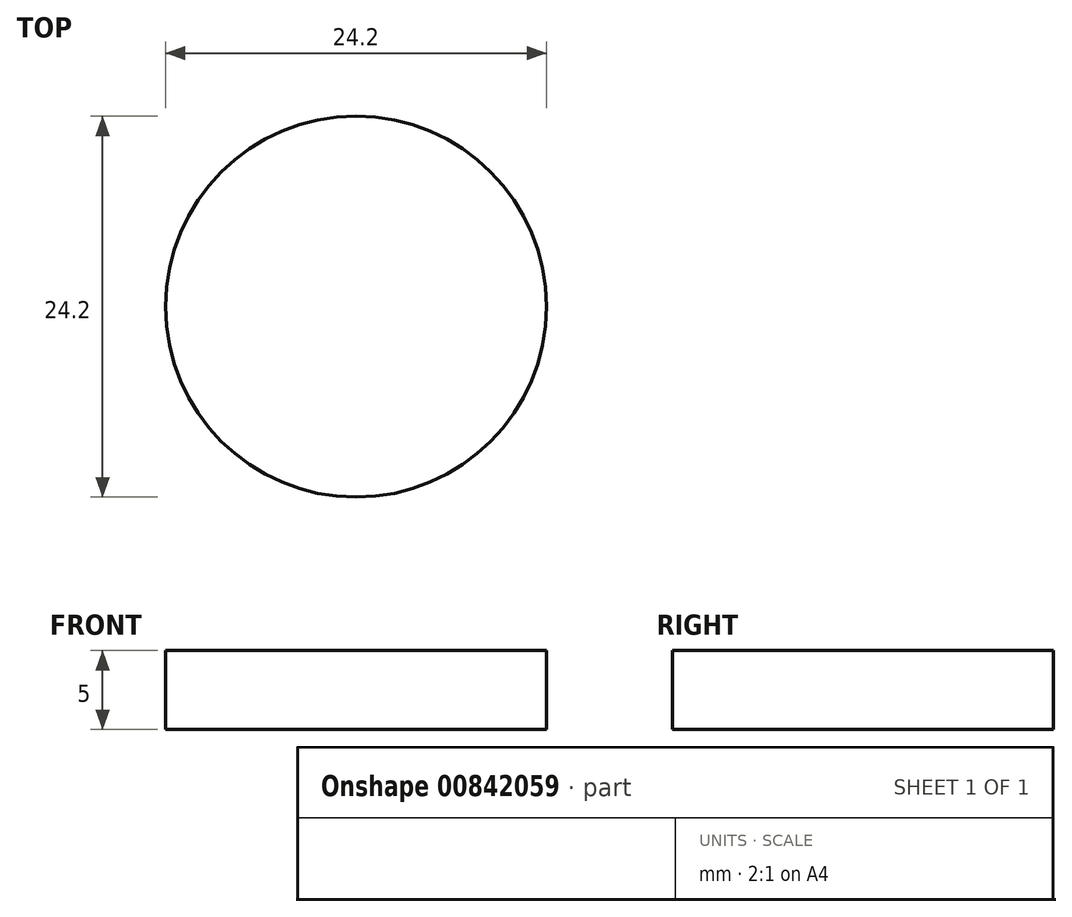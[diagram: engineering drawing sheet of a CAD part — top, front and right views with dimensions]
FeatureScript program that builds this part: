
annotation { "Feature Type Name" : "Feature", "Feature Type Description" : "" }
export const myFeature = defineFeature(function(context is Context, id is Id, definition is map)
    precondition{}
    {
        {
            var Q0;
            Q0=qCreatedBy(makeId("Top.planeOp"),FACE);
            var sketch = newSketch(context, id + "F0", { "sketchPlane" : qUnion([Q0])});
            skCircle(sketch, "E0", {"center": v(0, 0) * mm, "radius": 12.1 * mm});
            skSolve(sketch);
        }
        {
            var Q0;
            Q0 = qSketchRegion(id + "F0", true);
            extrude(context, id + "F1", {"entities" : qUnion([Q0]), "depth" : 5 * mm, "offsetDistance" : 25 * mm});
        }
    });
